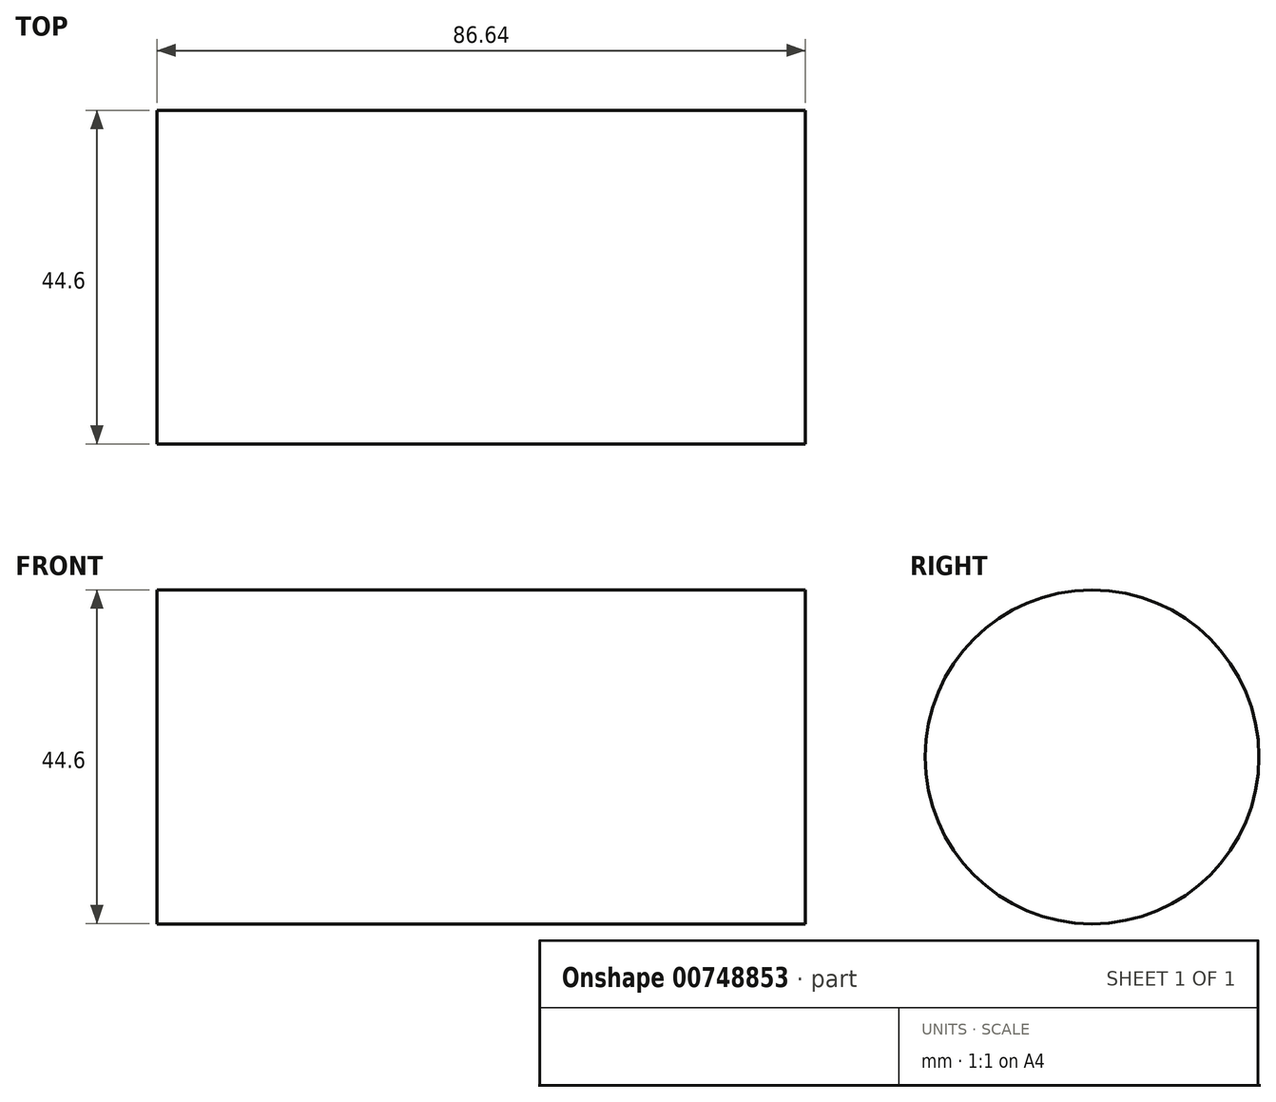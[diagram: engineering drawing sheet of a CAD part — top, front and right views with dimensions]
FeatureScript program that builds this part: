
annotation { "Feature Type Name" : "Feature", "Feature Type Description" : "" }
export const myFeature = defineFeature(function(context is Context, id is Id, definition is map)
    precondition{}
    {
        {
            var Q0;
            Q0=qCreatedBy(makeId("Right.planeOp"),FACE);
            var sketch = newSketch(context, id + "F0", { "sketchPlane" : qUnion([Q0])});
            skCircle(sketch, "E0", {"center": v(0, -77.21) * mm, "radius": 22.3 * mm});
            skSolve(sketch);
        }
        {
            var Q0;
            Q0 = qSketchRegion(id + "F0", true);
            extrude(context, id + "F1", {"entities" : qUnion([Q0]), "depth" : 86.64 * mm, "offsetDistance" : 25.4 * mm});
        }
    });
